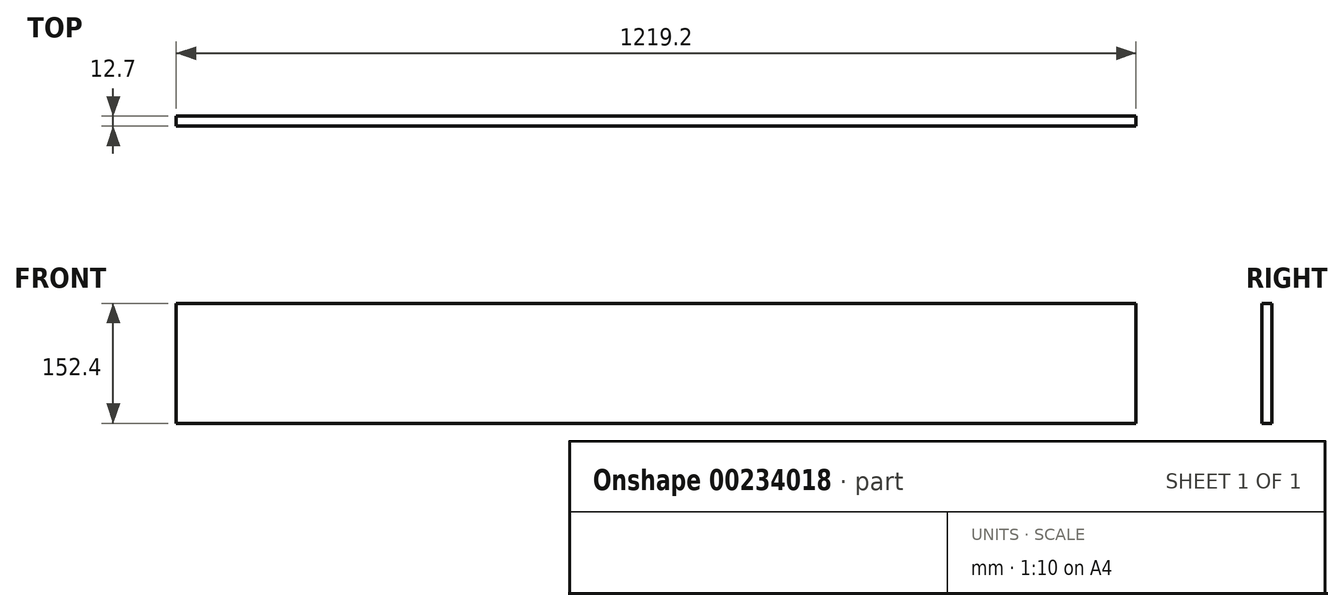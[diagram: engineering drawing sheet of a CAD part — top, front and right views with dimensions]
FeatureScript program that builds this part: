
annotation { "Feature Type Name" : "Feature", "Feature Type Description" : "" }
export const myFeature = defineFeature(function(context is Context, id is Id, definition is map)
    precondition{}
    {
        {
            var Q0;
            Q0=qCreatedBy(makeId("Front.planeOp"),FACE);
            var sketch = newSketch(context, id + "F0", { "sketchPlane" : qUnion([Q0])});
            skLineSegment(sketch, "E0.bottom", {"start": v(-607.04, 8.06) * mm, "end": v(612.16, 8.06) * mm});
            skLineSegment(sketch, "E0.top", {"start": v(-607.04, -144.34) * mm, "end": v(612.16, -144.34) * mm});
            skLineSegment(sketch, "E0.left", {"start": v(-607.04, 8.06) * mm, "end": v(-607.04, -144.34) * mm});
            skLineSegment(sketch, "E0.right", {"start": v(612.16, 8.06) * mm, "end": v(612.16, -144.34) * mm});
            skSolve(sketch);
        }
        {
            var Q0;
            Q0 = qSketchRegion(id + "F0", true);
            extrude(context, id + "F1", {"entities" : qUnion([Q0]), "depth" : 12.7 * mm});
        }
    });
